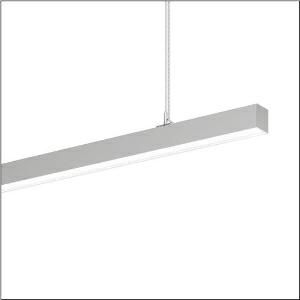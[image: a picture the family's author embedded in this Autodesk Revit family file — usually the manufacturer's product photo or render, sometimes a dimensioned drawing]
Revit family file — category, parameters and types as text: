
# Revit family: silica_r__21_51mx33dc4dsb_9471
name_source: partatom
category: Lighting Fixtures
units: mm (PartAtom-declared; Revit-internal decimal feet)

## family parameters
Cut with Voids When Loaded = No
Host = Face
Light Source = No
Part Type = Normal
Room Calculation Point = No
Round Connector Dimension = Use Diameter
Shared = No

## types (1)
- --- (1 x LED, 14790 lm, 93.9 W, 4000K)
    Apparent Load = 94 VA
    CIE Flux Codes = 78 96 99 55 100
    Color Rendering = 80
    Color Temperature = 4000K
    Default Elevation = 1800 mm
    Description = Silica® 21, office luminaire, primary optical cover: prismatic diffuser, of PMMA, CAT 2 (L<= 3000cd/m²), light emission: direct/indirect distribution, primary light characteristic: symmetric, installation type: suspended mounting, LED, rated luminous flux: 14.790lm, luminous efficacy: 158lm/W, light colour: 840, colour temperature: 4000K, with terminal, 3+2-pole, max. 2.5mm², mains connection: 220..240V, AC, 50/60Hz, rated input power: 93.9W, luminaire housing, of aluminium, metallic grey (RAL 9006), length: 3.004mm, width: 53mm, height: 53mm, protection rating (complete): IP20, insulation class (complete): insulation class I (protective earthing), certification: CE, permissible operating ambient temperature: 0..+35°C, standard: EN 50419, packaging unit: 1 piece
    Height = 53 mm
    Lamp = 1 x LED
    Lamp Light Flux = 14790 lm
    Lamp Power = 93.9 W
    Lamp count = 1
    Length = 3004 mm
    Luminous efficacy = 158 lm/W
    Manufacturer = Siteco
    ModVariant = No
    Model = 51MX33DC4DSB
    Mounting Place = Ceiling
    Mounting Type = Pendant
    Number of Poles = 1
    OnlyDefault = Yes
    Power Factor = 1
    Product Name = Silica® 21
    Product group = office luminaire | ceiling pendant
    ProductGroupID = 902
    Protection Class = Protection class I
    Protection Degree = IP 20
    RLX_Detail_Level = 1
    RLX_Emergency_Light_Flux = 0 lm
    RLX_Emergency_Type = 0
    RLX_Emergency_Type_DB = No
    RlxData = <blob elided: 23373 chars, md5=f1ea1a07>
    Socket = socket
    Standby Power = 0 W
    System Light Flux = 14790 lm
    System Power = 94 W
    Type Comments = factory setting: luminous flux: 100 % | dim-lin: 254 | 323 mA
    Type Image = l_1297747.jpg
    URL = http://relux.com
    VarID = @adj_048863
    Voltage = 0 V
    Weight = 0.00 kg
    Width = 53 mm

## geometry (parser evidence)
native form markers: Blend x4, Sweep x14
no freeform markers — native parametric forms only
